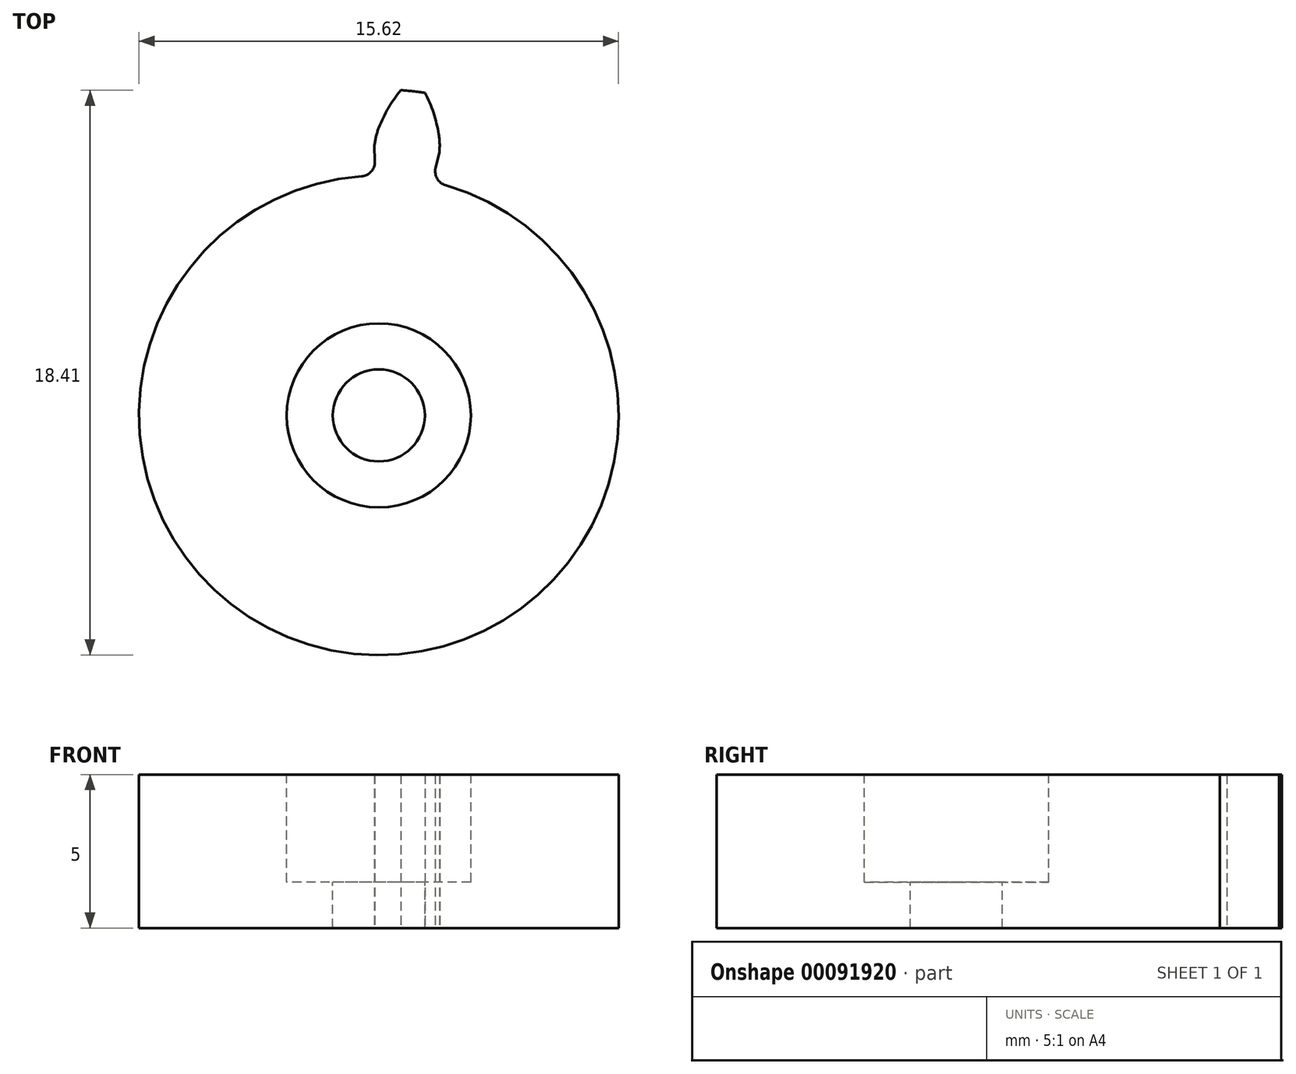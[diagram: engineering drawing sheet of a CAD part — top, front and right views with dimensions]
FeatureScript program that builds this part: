
annotation { "Feature Type Name" : "Feature", "Feature Type Description" : "" }
export const myFeature = defineFeature(function(context is Context, id is Id, definition is map)
    precondition{}
    {
        {
            var Q0;
            Q0=qCreatedBy(makeId("Front.planeOp"),FACE);
            var sketch = newSketch(context, id + "F0", { "sketchPlane" : qUnion([Q0])});
            skLineSegment(sketch, "E0", {"start": v(0, 72.27) * mm, "end": v(0, -50.25) * mm, "construction": true});
            skSolve(sketch);
        }
        {
            var Q0;
            Q0=qCreatedBy(makeId("Top.planeOp"),FACE);
            var sketch = newSketch(context, id + "F1", { "sketchPlane" : qUnion([Q0])});
            skCircle(sketch, "E1", {"center": v(0, 0) * mm, "radius": 9.38 * mm, "construction": true});
            skCircle(sketch, "E2", {"center": v(0, 0) * mm, "radius": 7.81 * mm});
            skSolve(sketch);
        }
        {
            var Q0;
            Q0 = qSketchRegion(id + "F1", true);
            extrude(context, id + "F2", {"entities" : qUnion([Q0]), "depth" : 5 * mm});
        }
        {
            var Q0;
            Q0=qCreatedBy(makeId("Top.planeOp"),FACE);
            var sketch = newSketch(context, id + "F3", { "sketchPlane" : qUnion([Q0])});
            skLineSegment(sketch, "E3", {"start": v(0, 0) * mm, "end": v(0, 29.7) * mm, "construction": true});
            skLineSegment(sketch, "E4", {"start": v(0, 0) * mm, "end": v(-10.47, 28.76) * mm, "construction": true});
            skLineSegment(sketch, "E5", {"start": v(0, 9.38) * mm, "end": v(-3.01, 8.28) * mm, "construction": true});
            skCircle(sketch, "E6", {"center": v(0, 0) * mm, "radius": 9.38 * mm, "construction": true});
            skCircle(sketch, "E7", {"center": v(0, 0) * mm, "radius": 10.62 * mm, "construction": true});
            skArc(sketch, "E8", {"start": v(-0.57, 7.8) * mm, "mid": v(-0.82, -7.77) * mm, "end": v(2.18, 7.5) * mm, "construction": true});
            skCircle(sketch, "E9", {"center": v(0, 0) * mm, "radius": 8.8 * mm, "construction": true});
            skCircle(sketch, "E10", {"center": v(4.37, 7.65) * mm, "radius": 4.7 * mm, "construction": true});
            skCircle(sketch, "E11", {"center": v(2.04, 8.57) * mm, "radius": 2.2 * mm, "construction": true});
            skArc(sketch, "E12", {"start": v(0.71, 10.6) * mm, "mid": v(0.31, 10.02) * mm, "end": v(0, 9.38) * mm});
            skArc(sketch, "E13", {"start": v(0, 9.38) * mm, "mid": v(-0.09, 9.1) * mm, "end": v(-0.14, 8.8) * mm});
            skLineSegment(sketch, "E14", {"start": v(-0.14, 8.8) * mm, "end": v(-0.13, 8.27) * mm});
            skLineSegment(sketch, "E15", {"start": v(-0.12, 7.81) * mm, "end": v(0, 0) * mm, "construction": true});
            skArc(sketch, "E16", {"start": v(1.95, 9.17) * mm, "mid": v(0.98, 9.32) * mm, "end": v(0, 9.38) * mm});
            skLineSegment(sketch, "E17", {"start": v(0, 0) * mm, "end": v(0.98, 9.32) * mm, "construction": true});
            skLineSegment(sketch, "E18", {"start": v(0.98, 9.32) * mm, "end": v(1.35, 12.8) * mm, "construction": true});
            skArc(sketch, "E19", {"start": v(1.11, 10.57) * mm, "mid": v(0.91, 10.59) * mm, "end": v(0.71, 10.6) * mm});
            skArc(sketch, "E20.MirrorCS", {"start": v(1.11, 10.57) * mm, "mid": v(1.31, 10.54) * mm, "end": v(1.5, 10.52) * mm});
            skArc(sketch, "E21.MirrorCS", {"start": v(1.5, 10.52) * mm, "mid": v(1.78, 9.86) * mm, "end": v(1.95, 9.17) * mm});
            skArc(sketch, "E22.MirrorCS", {"start": v(1.95, 9.17) * mm, "mid": v(1.98, 8.88) * mm, "end": v(1.97, 8.59) * mm});
            skLineSegment(sketch, "E23.MirrorCS", {"start": v(1.97, 8.59) * mm, "end": v(1.85, 8.06) * mm});
            skPoint(sketch, "E24.visualSharp", {"position": v(-0.12, 7.81) * mm});
            skArc(sketch, "E24.filletArc", {"start": v(-0.57, 7.8) * mm, "mid": v(-0.25, 7.94) * mm, "end": v(-0.13, 8.27) * mm});
            skArc(sketch, "E25.MirrorCS", {"start": v(2.18, 7.5) * mm, "mid": v(1.9, 7.72) * mm, "end": v(1.85, 8.06) * mm});
            skPoint(sketch, "E26.orphan", {"position": v(1.75, 7.61) * mm});
            skArc(sketch, "E27", {"start": v(-0.57, 7.8) * mm, "mid": v(0.82, 7.77) * mm, "end": v(2.18, 7.5) * mm});
            skSolve(sketch);
        }
        {
            var Q0;
            Q0 = qSketchRegion(id + "F3", true);
            extrude(context, id + "F4", {"entities" : qUnion([Q0]), "operationType" : NewBodyOperationType.ADD, "depth" : 5 * mm});
        }
        {
            var Q0;
            {var subQ0=sQuery(id+"F3.wireOp",EDGE,"E27");var subQ1=sQuery(id+"F3.wireOp",EDGE,"E25.MirrorCS");var subQ2=sQuery(id+"F3.wireOp",EDGE,"E24.filletArc");var subQ3=sQuery(id+"F3.wireOp",EDGE,"E23.MirrorCS");var subQ4=sQuery(id+"F3.wireOp",EDGE,"E22.MirrorCS");var subQ5=sQuery(id+"F3.wireOp",EDGE,"E21.MirrorCS");var subQ6=sQuery(id+"F3.wireOp",EDGE,"E20.MirrorCS");var subQ7=sQuery(id+"F3.wireOp",EDGE,"E19");var subQ8=sQuery(id+"F3.wireOp",EDGE,"E14");var subQ9=sQuery(id+"F3.wireOp",EDGE,"E13");var subQ10=sQuery(id+"F3.wireOp",EDGE,"E12");Q0=makeQuery(id+"FKo0gFQ4KOUnKrD_1.14.F4.boolean.opBoolean","MERGE",FACE,{"derivedFrom":[makeQuery(id+"FKo0gFQ4KOUnKrD_1.13.F4.boolean.opBoolean","MERGE",FACE,{"derivedFrom":[makeQuery(id+"FKo0gFQ4KOUnKrD_1.12.F4.boolean.opBoolean","MERGE",FACE,{"derivedFrom":[makeQuery(id+"FKo0gFQ4KOUnKrD_1.11.F4.boolean.opBoolean","MERGE",FACE,{"derivedFrom":[makeQuery(id+"FKo0gFQ4KOUnKrD_1.10.F4.boolean.opBoolean","MERGE",FACE,{"derivedFrom":[makeQuery(id+"FKo0gFQ4KOUnKrD_1.9.F4.boolean.opBoolean","MERGE",FACE,{"derivedFrom":[makeQuery(id+"FKo0gFQ4KOUnKrD_1.8.F4.boolean.opBoolean","MERGE",FACE,{"derivedFrom":[makeQuery(id+"FKo0gFQ4KOUnKrD_1.7.F4.boolean.opBoolean","MERGE",FACE,{"derivedFrom":[makeQuery(id+"FKo0gFQ4KOUnKrD_1.6.F4.boolean.opBoolean","MERGE",FACE,{"derivedFrom":[makeQuery(id+"FKo0gFQ4KOUnKrD_1.5.F4.boolean.opBoolean","MERGE",FACE,{"derivedFrom":[makeQuery(id+"FKo0gFQ4KOUnKrD_1.4.F4.boolean.opBoolean","MERGE",FACE,{"derivedFrom":[makeQuery(id+"FKo0gFQ4KOUnKrD_1.3.F4.boolean.opBoolean","MERGE",FACE,{"derivedFrom":[makeQuery(id+"FKo0gFQ4KOUnKrD_1.2.F4.boolean.opBoolean","MERGE",FACE,{"derivedFrom":[makeQuery(id+"FKo0gFQ4KOUnKrD_1.1.F4.boolean.opBoolean","MERGE",FACE,{"derivedFrom":[makeQuery(id+"F4.boolean.opBoolean","MERGE",FACE,{"derivedFrom":[makeQuery(id+"F2.opExtrude","CAP_FACE",FACE,{"disambiguationData":[OSD([sQuery(id+"F1.wireOp",EDGE,"E2")])],"isStart":false}),makeQuery(id+"F4.opExtrude","CAP_FACE",FACE,{"disambiguationData":[OSD([subQ10,subQ9,subQ8,subQ7,subQ6,subQ5,subQ4,subQ3,subQ2,subQ1,subQ0])],"isStart":false})]}),makeQuery(id+"FKo0gFQ4KOUnKrD_1.1.F4.opExtrude","CAP_FACE",FACE,{"disambiguationData":[OSD([subQ10,subQ9,subQ8,subQ7,subQ6,subQ5,subQ4,subQ3,subQ2,subQ1,subQ0])],"isStart":false})]}),makeQuery(id+"FKo0gFQ4KOUnKrD_1.2.F4.opExtrude","CAP_FACE",FACE,{"disambiguationData":[OSD([subQ10,subQ9,subQ8,subQ7,subQ6,subQ5,subQ4,subQ3,subQ2,subQ1,subQ0])],"isStart":false})]}),makeQuery(id+"FKo0gFQ4KOUnKrD_1.3.F4.opExtrude","CAP_FACE",FACE,{"disambiguationData":[OSD([subQ10,subQ9,subQ8,subQ7,subQ6,subQ5,subQ4,subQ3,subQ2,subQ1,subQ0])],"isStart":false})]}),makeQuery(id+"FKo0gFQ4KOUnKrD_1.4.F4.opExtrude","CAP_FACE",FACE,{"disambiguationData":[OSD([subQ10,subQ9,subQ8,subQ7,subQ6,subQ5,subQ4,subQ3,subQ2,subQ1,subQ0])],"isStart":false})]}),makeQuery(id+"FKo0gFQ4KOUnKrD_1.5.F4.opExtrude","CAP_FACE",FACE,{"disambiguationData":[OSD([subQ10,subQ9,subQ8,subQ7,subQ6,subQ5,subQ4,subQ3,subQ2,subQ1,subQ0])],"isStart":false})]}),makeQuery(id+"FKo0gFQ4KOUnKrD_1.6.F4.opExtrude","CAP_FACE",FACE,{"disambiguationData":[OSD([subQ10,subQ9,subQ8,subQ7,subQ6,subQ5,subQ4,subQ3,subQ2,subQ1,subQ0])],"isStart":false})]}),makeQuery(id+"FKo0gFQ4KOUnKrD_1.7.F4.opExtrude","CAP_FACE",FACE,{"disambiguationData":[OSD([subQ10,subQ9,subQ8,subQ7,subQ6,subQ5,subQ4,subQ3,subQ2,subQ1,subQ0])],"isStart":false})]}),makeQuery(id+"FKo0gFQ4KOUnKrD_1.8.F4.opExtrude","CAP_FACE",FACE,{"disambiguationData":[OSD([subQ10,subQ9,subQ8,subQ7,subQ6,subQ5,subQ4,subQ3,subQ2,subQ1,subQ0])],"isStart":false})]}),makeQuery(id+"FKo0gFQ4KOUnKrD_1.9.F4.opExtrude","CAP_FACE",FACE,{"disambiguationData":[OSD([subQ10,subQ9,subQ8,subQ7,subQ6,subQ5,subQ4,subQ3,subQ2,subQ1,subQ0])],"isStart":false})]}),makeQuery(id+"FKo0gFQ4KOUnKrD_1.10.F4.opExtrude","CAP_FACE",FACE,{"disambiguationData":[OSD([subQ10,subQ9,subQ8,subQ7,subQ6,subQ5,subQ4,subQ3,subQ2,subQ1,subQ0])],"isStart":false})]}),makeQuery(id+"FKo0gFQ4KOUnKrD_1.11.F4.opExtrude","CAP_FACE",FACE,{"disambiguationData":[OSD([subQ10,subQ9,subQ8,subQ7,subQ6,subQ5,subQ4,subQ3,subQ2,subQ1,subQ0])],"isStart":false})]}),makeQuery(id+"FKo0gFQ4KOUnKrD_1.12.F4.opExtrude","CAP_FACE",FACE,{"disambiguationData":[OSD([subQ10,subQ9,subQ8,subQ7,subQ6,subQ5,subQ4,subQ3,subQ2,subQ1,subQ0])],"isStart":false})]}),makeQuery(id+"FKo0gFQ4KOUnKrD_1.13.F4.opExtrude","CAP_FACE",FACE,{"disambiguationData":[OSD([subQ10,subQ9,subQ8,subQ7,subQ6,subQ5,subQ4,subQ3,subQ2,subQ1,subQ0])],"isStart":false})]}),makeQuery(id+"FKo0gFQ4KOUnKrD_1.14.F4.opExtrude","CAP_FACE",FACE,{"disambiguationData":[OSD([subQ10,subQ9,subQ8,subQ7,subQ6,subQ5,subQ4,subQ3,subQ2,subQ1,subQ0])],"isStart":false})]});}
            var sketch = newSketch(context, id + "F5", { "sketchPlane" : qUnion([Q0])});
            skCircle(sketch, "E28", {"center": v(0, 0) * mm, "radius": 3 * mm});
            skSolve(sketch);
        }
        {
            var Q0;
            Q0 = qSketchRegion(id + "F5", true);
            extrude(context, id + "F6", {"entities" : qUnion([Q0]), "operationType" : NewBodyOperationType.REMOVE, "oppositeDirection" : true, "depth" : 3.5 * mm});
        }
        {
            var Q0;
            Q0=makeQuery(id+"F6.boolean.opBoolean","COPY",FACE,{"derivedFrom":makeQuery(id+"F6.opExtrude","CAP_FACE",FACE,{"disambiguationData":[OSD([sQuery(id+"F5.wireOp",EDGE,"E28")])],"isStart":false})});
            var sketch = newSketch(context, id + "F7", { "sketchPlane" : qUnion([Q0])});
            skCircle(sketch, "E29", {"center": v(0, 0) * mm, "radius": 1.5 * mm});
            skSolve(sketch);
        }
        {
            var Q0;
            Q0 = qSketchRegion(id + "F7", true);
            extrude(context, id + "F8", {"entities" : qUnion([Q0]), "operationType" : NewBodyOperationType.REMOVE, "endBound" : BoundingType.THROUGH_ALL, "oppositeDirection" : true, "depth" : 25 * mm});
        }
    });
